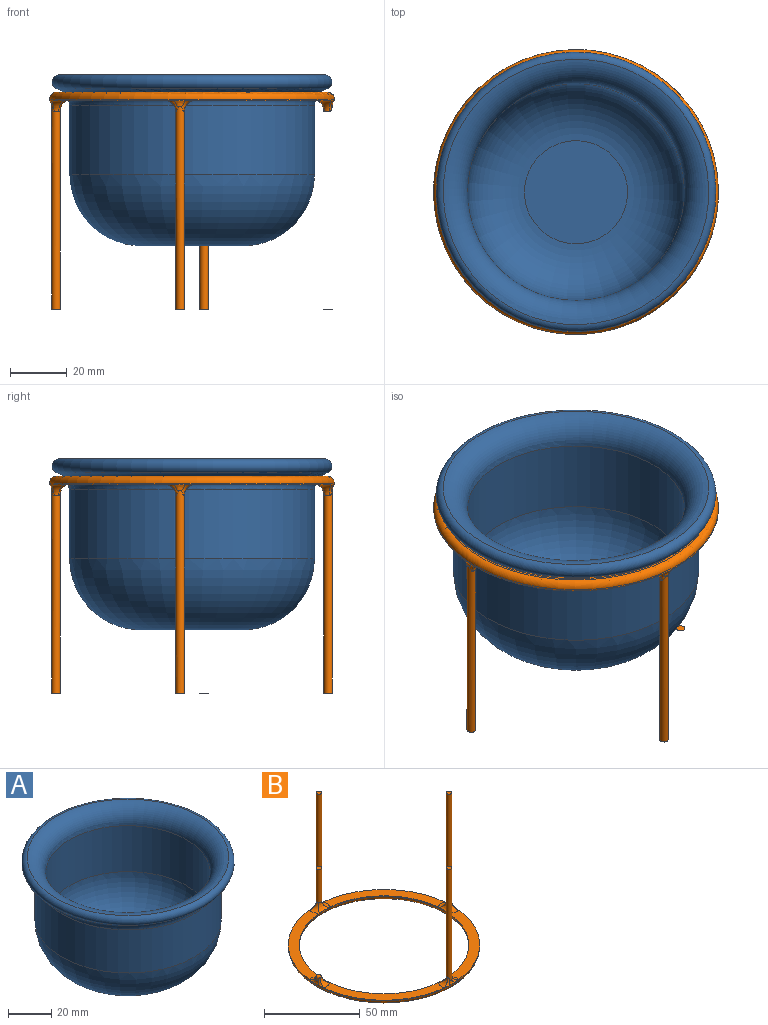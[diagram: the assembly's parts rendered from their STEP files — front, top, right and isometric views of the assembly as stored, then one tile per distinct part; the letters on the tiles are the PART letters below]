
ASSEMBLY  parts=2 mates=1
PART A: 9 faces, bbox 106.3x106.3x60 mm
  f0: plane 36.2x36.2mm, normal (0,0,-1), area 1029.2mm2, adj f1
  f1: torus R=18.1mm, axis (0,0,1), area 8393mm2, adj f0,f2
  f2: cylinder r=43.1mm len=86.2mm, axis (0,0,1), area 6601.1mm2, adj f1,f7
  f3: cylinder r=38.1mm len=76.2mm, axis (0,0,1), area 6227.5mm2, adj f4,f8
  f4: torus R=18.1mm, axis (0,0,1), area 6086.1mm2, adj f3,f5
  f5: plane 36.2x36.2mm, normal (0,0,1), area 1029.2mm2, adj f4
  f6: torus R=46.6mm, axis (0,0,-1), area 2157.9mm2, adj f7,f8
  f7: torus R=49.1mm, axis (0,0,1), area 2138.8mm2, adj f2,f6
  f8: torus R=47.1mm, axis (0,0,1), area 3527.5mm2, adj f3,f6
PART B: 42 faces, bbox 114.2x114.2x82.2 mm
  f0: bspline ~5.19x2.82mm, area 6.2mm2, adj f1,f2,f3,f4
  f1: cylinder r=1.5mm len=70.68mm, axis (0,0,-1), area 655.9mm2, adj f0,f2,f4,f5,f6,f7,f8
  f2: bspline ~4.64x4mm, area 6.5mm2, adj f0,f1,f3,f5
  f3: cylinder r=50mm len=100mm, axis (0,0,-1), area 157.1mm2, adj f0,f2,f4,f9,f10,f11,f12,f13
  f4: bspline ~4.64x4mm, area 6.5mm2, adj f0,f1,f3,f7
  f5: torus R=5.5mm, axis (0,0,-1), area 20.6mm2, adj f1,f2,f6,f12
  f6: bspline ~7.72x4mm, area 19.6mm2, adj f1,f5,f7,f23
  f7: torus R=5.5mm, axis (0,0,-1), area 20.6mm2, adj f1,f4,f6,f13
  f8: plane 3x3mm, normal (0,0,1), area 7.1mm2, adj f1
  f9: torus R=47.5mm, axis (0,0,1), area 1211.3mm2, adj f3,f24
  f10: bspline ~5.19x2.82mm, area 6.2mm2, adj f3,f11,f22,f25
  f11: bspline ~4.64x4mm, area 6.5mm2, adj f3,f10,f25,f26
  f12: plane 45.87x45.87mm, normal (0,0,1), area 366.8mm2, adj f3,f5,f23,f26
  f13: plane 45.87x45.87mm, normal (0,0,1), area 366.8mm2, adj f3,f7,f23,f27
  f14: bspline ~4.63x4mm, area 6.5mm2, adj f3,f15,f27,f28
  f15: bspline ~5.19x2.82mm, area 6.2mm2, adj f3,f14,f16,f28
  f16: bspline ~4.64x4mm, area 6.5mm2, adj f3,f15,f28,f29
  f17: plane 45.87x45.87mm, normal (0,0,1), area 366.8mm2, adj f3,f23,f29,f30
  f18: bspline ~4.63x4mm, area 6.5mm2, adj f3,f19,f30,f31
  f19: bspline ~5.19x2.82mm, area 6.2mm2, adj f3,f18,f20,f31
  f20: bspline ~4.64x4mm, area 6.5mm2, adj f3,f19,f31,f32
  f21: plane 45.87x45.87mm, normal (0,0,1), area 366.8mm2, adj f3,f23,f32,f33
  f22: bspline ~4.64x4mm, area 6.5mm2, adj f3,f10,f25,f33
  f23: cylinder r=44.25mm len=88.5mm, axis (0,0,-1), area 139mm2, adj f6,f12,f13,f17,f21,f34,f35,f36
  f24: plane 95x95mm, normal (0,0,-1), area 222.1mm2, adj f9,f34
  f25: cylinder r=1.5mm len=2.92mm, axis (0,0,-1), area 3.7mm2, adj f10,f11,f22,f26,f33,f37
  f26: torus R=5.5mm, axis (0,0,-1), area 20.6mm2, adj f11,f12,f25,f37
  f27: torus R=5.5mm, axis (0,0,-1), area 20.6mm2, adj f13,f14,f28,f35
  f28: cylinder r=1.5mm len=71.26mm, axis (0,0,-1), area 656.3mm2, adj f14,f15,f16,f27,f29,f35,f38
  f29: torus R=5.5mm, axis (0,0,-1), area 20.6mm2, adj f16,f17,f28,f35
  f30: torus R=5.5mm, axis (0,0,-1), area 20.6mm2, adj f17,f18,f31,f36
  f31: cylinder r=1.5mm len=71.26mm, axis (0,0,-1), area 656.8mm2, adj f18,f19,f20,f30,f32,f36,f39
  f32: torus R=5.5mm, axis (0,0,-1), area 20.6mm2, adj f20,f21,f31,f36
  f33: torus R=5.5mm, axis (0,0,-1), area 20.6mm2, adj f21,f22,f25,f37
  f34: torus R=46.75mm, axis (0,0,1), area 1114.2mm2, adj f23,f24
  f35: bspline ~7.72x4mm, area 19.6mm2, adj f23,f27,f28,f29
  f36: bspline ~7.72x4mm, area 19.6mm2, adj f23,f30,f31,f32
  f37: bspline ~7.72x4mm, area 19.6mm2, adj f23,f25,f26,f33
  f38: plane 3x3mm, normal (0,0,1), area 7.1mm2, adj f28
  f39: plane 3x3mm, normal (0,0,1), area 7.1mm2, adj f31
  f40: cylinder r=1.5mm len=1.38mm, axis (0,0,-1), area 0mm2, adj f41
  f41: plane 9x9mm, normal (0,0,1), area 7.1mm2, adj f40
PLACE A rot(axis=(0,0,-1),5deg) t=(-88.06,-2.47,-11.14)mm
PLACE B rot(axis=(-0.04,-1,0),180deg) t=(-88.06,-2.47,23.83)mm
MATE cylindrical B.f3 <-> A.f1  axis (0,0,1) through (-88.06,-2.47,21.08)mm
